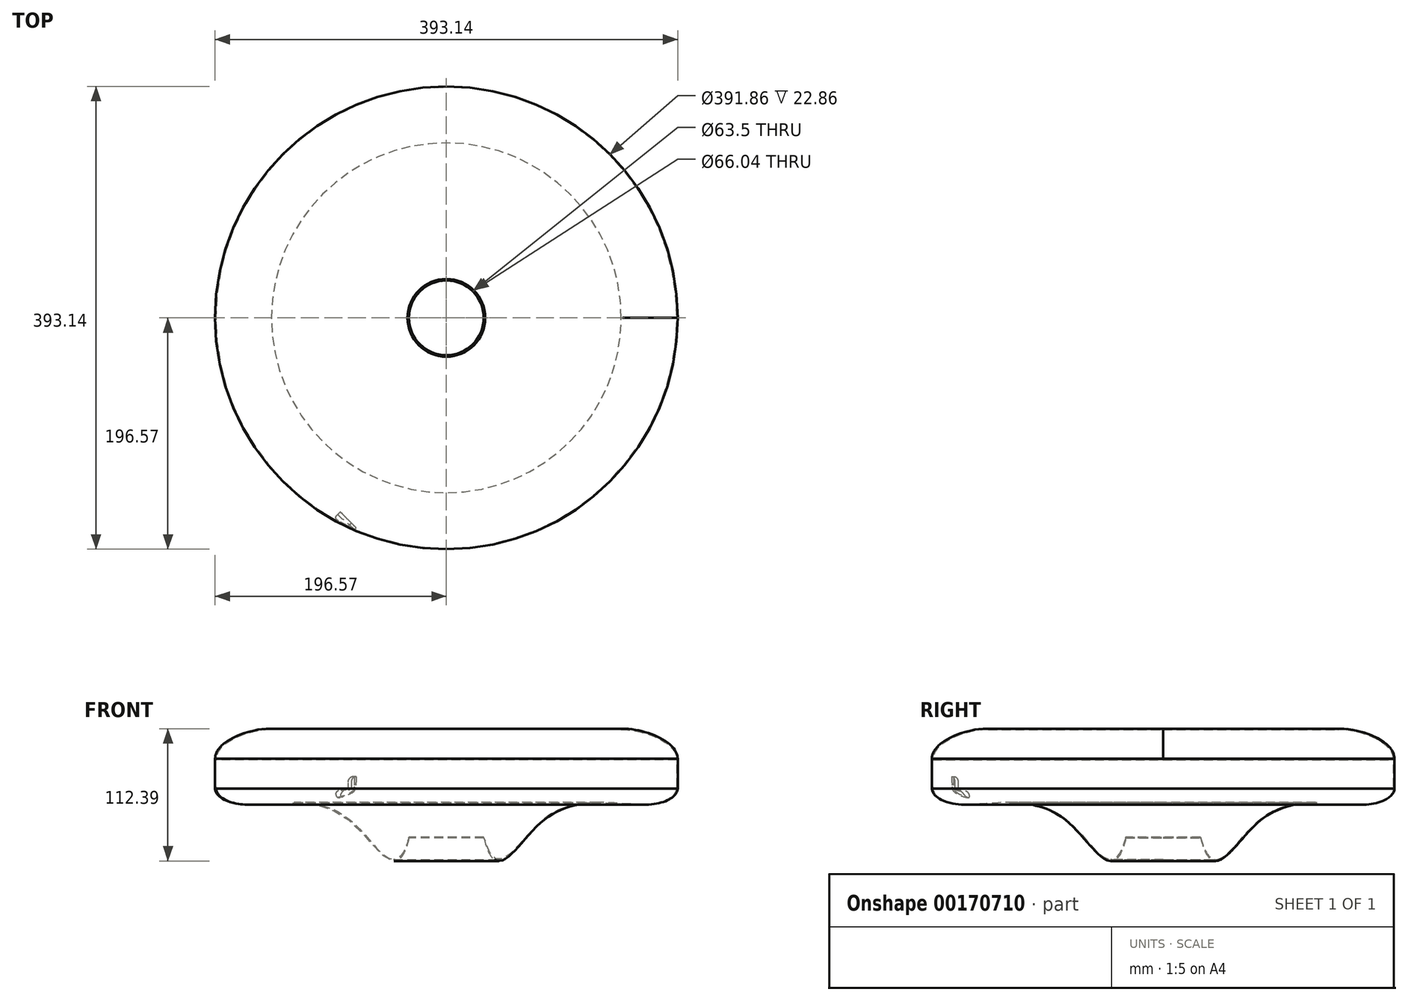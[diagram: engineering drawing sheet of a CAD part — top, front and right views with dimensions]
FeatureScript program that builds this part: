
annotation { "Feature Type Name" : "Feature", "Feature Type Description" : "" }
export const myFeature = defineFeature(function(context is Context, id is Id, definition is map)
    precondition{}
    {
        {
            var Q0;
            Q0=qCreatedBy(makeId("Front.planeOp"),FACE);
            var sketch = newSketch(context, id + "F0", { "sketchPlane" : qUnion([Q0])});
            skLineSegment(sketch, "E0", {"start": v(195.93, -25.43) * mm, "end": v(195.93, -48.3) * mm});
            skLineSegment(sketch, "E1", {"start": v(148.6, 0.52) * mm, "end": v(33.02, 0.52) * mm});
            skLineSegment(sketch, "E2", {"start": v(33.02, 0.52) * mm, "end": v(33.02, 1.16) * mm});
            skLineSegment(sketch, "E3", {"start": v(33.02, 1.16) * mm, "end": v(149.63, 1.16) * mm});
            skLineSegment(sketch, "E4", {"start": v(196.57, -49.9) * mm, "end": v(196.57, -24.5) * mm});
            skLineSegment(sketch, "E5", {"start": v(0, 0) * mm, "end": v(0, -95.36) * mm, "construction": true});
            skFitSpline(sketch, "E6", {"points": [v(31.75, -91.67) * mm, v(81.89, -77.29) * mm, v(172.8, -63.33) * mm, v(196.57, -49.9) * mm], "startDerivative": vector(98.46, -395.57) * mm, "endDerivative": vector(6.92, 88.44) * mm});
            skFitSpline(sketch, "E7", {"points": [v(195.93, -48.3) * mm, v(172.8, -63.17) * mm, v(81.89, -76.27) * mm, v(31.75, -91.03) * mm], "startDerivative": vector(-1.03, -105.83) * mm, "endDerivative": vector(-104.9, 387.65) * mm});
            skFitSpline(sketch, "E8", {"points": [v(148.6, 0.52) * mm, v(195.93, -25.43) * mm], "startDerivative": vector(62.95, -1.57) * mm, "endDerivative": vector(0, -44.04) * mm});
            skFitSpline(sketch, "E9", {"points": [v(196.57, -24.5) * mm, v(149.63, 1.16) * mm], "startDerivative": vector(0, 44.26) * mm, "endDerivative": vector(-59.52, 0) * mm});
            skLineSegment(sketch, "E10", {"start": v(31.75, -91.67) * mm, "end": v(31.75, -91.03) * mm});
            skSolve(sketch);
        }
        {
            var Q0;
            Q0=makeQuery(id+"F0.imprint","IMPRINT",FACE,{"disambiguationData":[TD([[makeQuery(id+"F0.imprint","IMPRINT",EDGE,{"derivedFrom":sQuery(id+"F0.wireOp",EDGE,"E0")}),1.0]])]});
            var Q1;
            Q1=sQuery(id+"F0.wireOp",EDGE,"E5");
            revolve(context, id + "F1", {"entities" : qUnion([Q0]), "axis" : qUnion([Q1]), "revolveType" : RevolveType.FULL});
        }
        {
            var Q0;
            Q0=qCreatedBy(makeId("Front.planeOp"),FACE);
            var Q1;
            Q1=qCreatedBy(makeId("Right.planeOp"),FACE);
            cPlane(context, id + "F2", {"entities" : qUnion([Q0, Q1]), "cplaneType" : CPlaneType.MID_PLANE, "offset" : 25.4 * mm, "width" : 152.4 * mm, "height" : 152.4 * mm});
        }
        {
            var Q0;
            Q0=qCreatedBy(id+"F2.planeOp",FACE);
            cPlane(context, id + "F3", {"entities" : qUnion([Q0]), "cplaneType" : CPlaneType.OFFSET, "offset" : 180.34 * mm, "width" : 152.4 * mm, "height" : 152.4 * mm});
        }
        {
            var Q0;
            Q0=qCreatedBy(id+"F3.planeOp",FACE);
            var sketch = newSketch(context, id + "F4", { "sketchPlane" : qUnion([Q0])});
            skFitSpline(sketch, "E11", {"points": [v(71.8, -39.5) * mm, v(70.5, -51.03) * mm, v(52.85, -57.4) * mm], "startDerivative": vector(-1.65, -55.88) * mm, "endDerivative": vector(-57, -10.9) * mm});
            skLineSegment(sketch, "E12", {"start": v(71.8, -39.5) * mm, "end": v(71.14, -39.5) * mm});
            skLineSegment(sketch, "E13", {"start": v(52.85, -57.4) * mm, "end": v(52.85, -56.73) * mm});
            skFitSpline(sketch, "E14", {"points": [v(67.6, -39.5) * mm, v(65.71, -49.53) * mm, v(52.85, -52.8) * mm], "startDerivative": vector(-19.73, -15.25) * mm, "endDerivative": vector(-23.87, -11.23) * mm});
            skArc(sketch, "E15.filletArc", {"start": v(57.32, -51.69) * mm, "mid": v(54.13, -53.36) * mm, "end": v(52.85, -56.73) * mm});
            skArc(sketch, "E16.filletArc", {"start": v(71.14, -39.5) * mm, "mid": v(67.44, -41.1) * mm, "end": v(66.07, -44.88) * mm});
            skSolve(sketch);
        }
        {
            var Q0;
            Q0=makeQuery(id+"F4.imprint","IMPRINT",FACE,{"disambiguationData":[TD([[makeQuery(id+"F4.imprint","IMPRINT",EDGE,{"derivedFrom":sQuery(id+"F4.wireOp",EDGE,"E11")}),-1.0]])]});
            extrude(context, id + "F5", {"entities" : qUnion([Q0]), "operationType" : NewBodyOperationType.ADD, "endBound" : BoundingType.UP_TO_NEXT, "depth" : 0.25 * mm});
        }
    });
